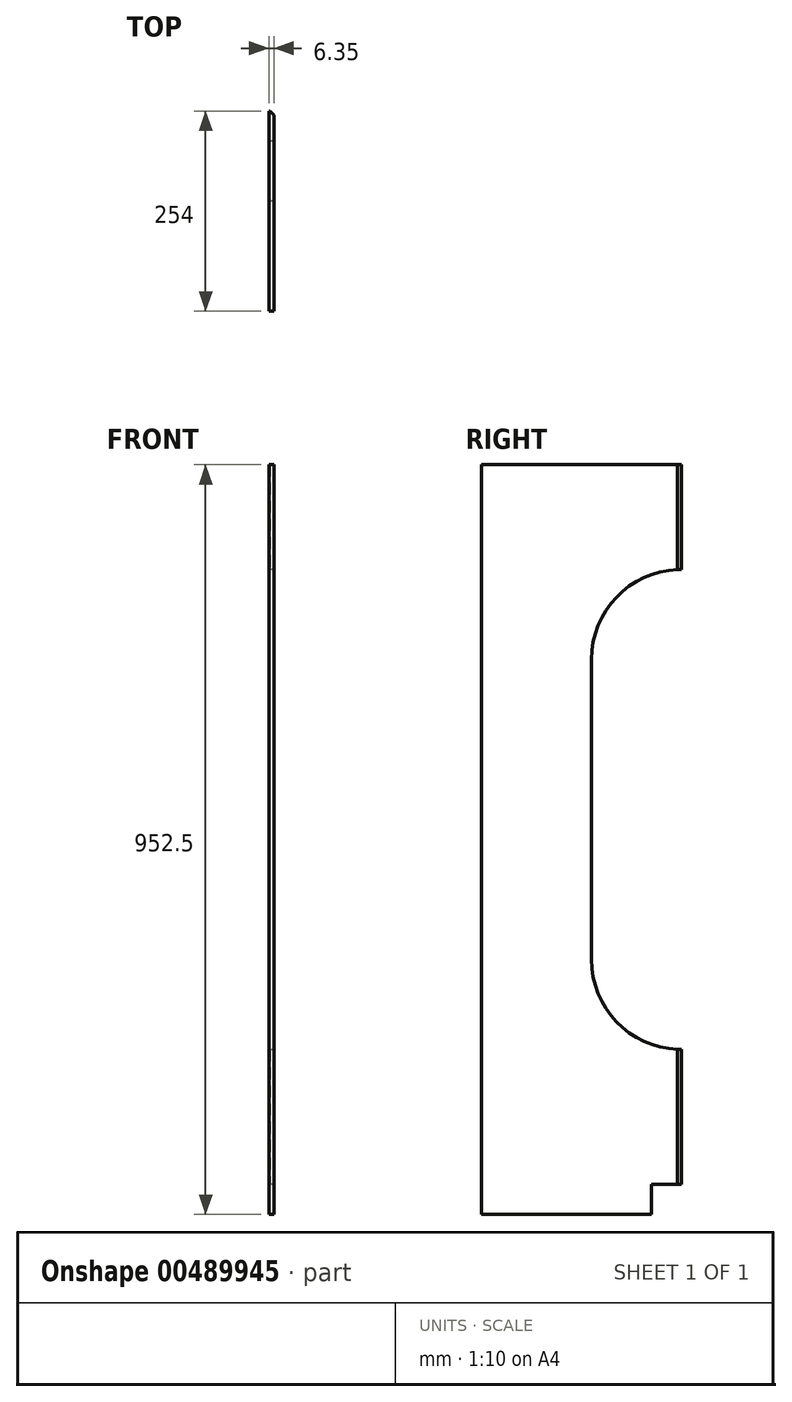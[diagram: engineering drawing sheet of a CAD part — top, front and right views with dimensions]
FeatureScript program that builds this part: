
annotation { "Feature Type Name" : "Feature", "Feature Type Description" : "" }
export const myFeature = defineFeature(function(context is Context, id is Id, definition is map)
    precondition{}
    {
        {
            var Q0;
            Q0=qCreatedBy(makeId("Right.planeOp"),FACE);
            var sketch = newSketch(context, id + "F0", { "sketchPlane" : qUnion([Q0])});
            skLineSegment(sketch, "E0.bottom", {"start": v(-127, 476.25) * mm, "end": v(127, 476.25) * mm});
            skLineSegment(sketch, "E0.top", {"start": v(-127, -476.25) * mm, "end": v(88.9, -476.25) * mm});
            skLineSegment(sketch, "E0.left", {"start": v(-127, 476.25) * mm, "end": v(-127, -476.25) * mm});
            skLineSegment(sketch, "E0.right", {"start": v(127, 476.25) * mm, "end": v(127, 342.9) * mm});
            skPoint(sketch, "E0.middle", {"position": v(0, 0) * mm});
            skLineSegment(sketch, "E1.0", {"start": v(127, 342.9) * mm, "end": v(127, 342.9) * mm});
            skLineSegment(sketch, "E2.0", {"start": v(12.7, 228.6) * mm, "end": v(12.7, -152.4) * mm});
            skLineSegment(sketch, "E3.0", {"start": v(127, -266.7) * mm, "end": v(127, -266.7) * mm});
            skLineSegment(sketch, "E4.trimOffspring", {"start": v(88.9, -438.15) * mm, "end": v(88.9, -476.25) * mm});
            skLineSegment(sketch, "E5.trimOffspring", {"start": v(88.9, -438.15) * mm, "end": v(127, -438.15) * mm});
            skPoint(sketch, "E6.orphan", {"position": v(127, -476.25) * mm});
            skLineSegment(sketch, "E7.trimOffspring", {"start": v(127, -266.7) * mm, "end": v(127, -438.15) * mm});
            skPoint(sketch, "E8.visualSharp", {"position": v(12.7, 342.9) * mm});
            skArc(sketch, "E8.filletArc", {"start": v(127, 342.9) * mm, "mid": v(46.18, 309.42) * mm, "end": v(12.7, 228.6) * mm});
            skPoint(sketch, "E9.visualSharp", {"position": v(12.7, -266.7) * mm});
            skArc(sketch, "E9.filletArc", {"start": v(12.7, -152.4) * mm, "mid": v(46.18, -233.22) * mm, "end": v(127, -266.7) * mm});
            skSolve(sketch);
        }
        {
            var Q0;
            Q0 = qSketchRegion(id + "F0", true);
            extrude(context, id + "F1", {"entities" : qUnion([Q0]), "depth" : 6.35 * mm});
        }
        {
            var Q0;
            Q0=makeQuery(id+"F1.opExtrude","CAP_EDGE",EDGE,{"disambiguationData":[OSD([sQuery(id+"F0.wireOp",EDGE,"E0.right")])],"isStart":false});
            var Q1;
            Q1=makeQuery(id+"F1.opExtrude","CAP_EDGE",EDGE,{"disambiguationData":[OSD([sQuery(id+"F0.wireOp",EDGE,"E7.trimOffspring")])],"isStart":false});
            chamfer(context, id + "F2", {"entities" : qUnion([Q0, Q1]), "width" : 4.76 * mm, "tangentPropagation" : true});
        }
    });
